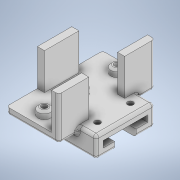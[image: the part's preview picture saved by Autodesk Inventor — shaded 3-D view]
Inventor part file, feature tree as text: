
AUTODESK INVENTOR PART (.ipt)
format: ipt  version: 2020.4 (Build 244396000, 396)  size: 340,992 bytes
history: native  units: in
note: dims shown in document units (in); Inventor stores cm internally (conversion verified against a paired STEP export)
features: extrude x10, sketch x10, chamfer x1, fillet x1
ambient origin geometry x8: Origin, YZ Plane, XZ Plane, XY Plane, X Axis, Y Axis, Z Axis, Center Point
bodies: Solid1 (feature_tree)
feature tree (22):
  extrude  "Extrusion1"  Depth=2.6378in
  extrude  "Extrusion2"  Depth=0.1969in
  extrude  "Extrusion6"  Depth=0.1969in
  extrude  "Extrusion8"  Depth=1.0in TaperAngle=0.0deg
  chamfer  "Chamfer1"  Distance=1.0in
  extrude  "Extrusion9"  Depth=0.3406in
  extrude  "Extrusion10"  Depth=0.1969in TaperAngle=0.0deg
  extrude  "Extrusion11"  Depth=0.1575in
  extrude  "Extrusion12"  Depth=0.1575in
  extrude  "Extrusion13"  Depth=0.0197in TaperAngle=0.0deg
  extrude  "Extrusion14"  Depth=0.0197in
  fillet  "Fillet4"  Radius=0.2362in
  sketch  "Sketch1"  dims[d0=1.4331in d1=2.6378in]
  sketch  "Sketch2"  dims[d2=0.1969in d3=0.0in d4=0.1969in]
  sketch  "Sketch6"  dims[d5=0.8268in d6=0.1969in]
  sketch  "Sketch8"  dims[d7=0.8268in d8=1.0in d9=0.0in]
  sketch  "Sketch9"  dims[d26=0.1969in]
  sketch  "Sketch10"  dims[d27=0.9449in d28=1.0in d29=0.0in]
  sketch  "Sketch11"  dims[d37=0.3406in d38=0.3406in]
  sketch  "Sketch12"  dims[d39=0.3406in d40=0.1969in d41=0.0in]
  sketch  "Sketch13"  dims[d42=0.0591in d43=0.0787in d44=45.0deg d45=0.1575in]
  sketch  "Sketch14"  dims[d46=0.1575in d47=0.1575in d48=0.7874in d49=0.0in d50=0.2362in d51=0.2362in d52=0.2362in d53=0.0984in d54=0.0in d55=1.6142in d56=0.1969in d57=0.5709in d58=0.1969in d59=0.4724in d60=0.1969in d61=0.4724in d62=0.1969in d63=0.5118in d64=1.4331in d65=0.0in d66=0.0in d67=0.1181in d68=0.1181in d69=1.4331in d70=0.0in d71=0.1575in d72=0.1575in d73=1.4331in d74=0.0in d75=0.0394in d76=0.0394in d77=0.5118in d78=0.0in d79=0.0787in d10=0.0197in d11=0.0344in d13=0.0197in d14=0.0344in d15=0.0197in d16=0.0344in]
